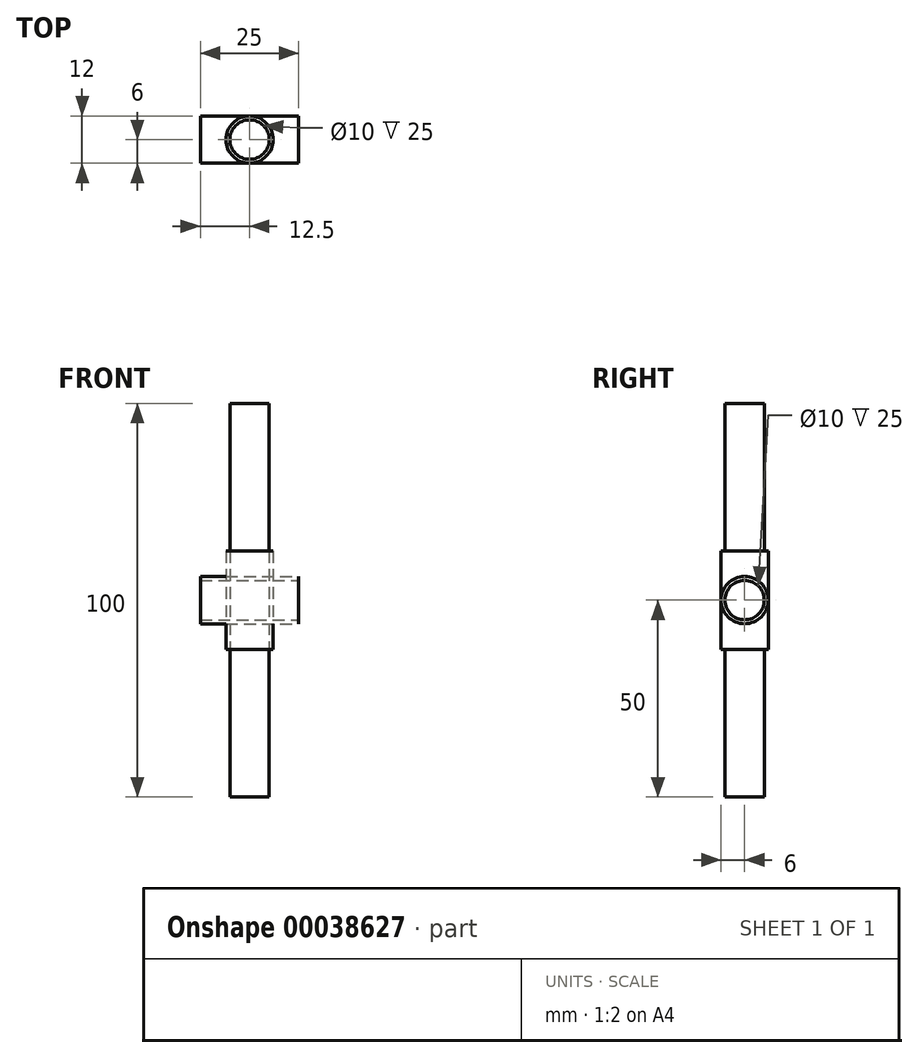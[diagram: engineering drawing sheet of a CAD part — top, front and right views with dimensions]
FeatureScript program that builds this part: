
annotation { "Feature Type Name" : "Feature", "Feature Type Description" : "" }
export const myFeature = defineFeature(function(context is Context, id is Id, definition is map)
    precondition{}
    {
        {
            var Q0;
            Q0=qCreatedBy(makeId("Top.planeOp"),FACE);
            var sketch = newSketch(context, id + "F0", { "sketchPlane" : qUnion([Q0])});
            skCircle(sketch, "E0", {"center": v(0, 0) * mm, "radius": 5 * mm});
            skCircle(sketch, "E1", {"center": v(0, 0) * mm, "radius": 6 * mm});
            skLineSegment(sketch, "E2", {"start": v(0, 0) * mm, "end": v(0, -6) * mm, "construction": true});
            skSolve(sketch);
        }
        {
            var Q0;
            Q0 = qSketchRegion(id + "F0", true);
            var Q1;
            Q1=makeQuery(id+"F0.imprint","IMPRINT",FACE,{"disambiguationData":[TD([[makeQuery(id+"F0.imprint","IMPRINT",EDGE,{"derivedFrom":sQuery(id+"F0.wireOp",EDGE,"E0")}),-1.0]])]});
            extrude(context, id + "F1", {"entities" : qUnion([Q0, Q1]), "endBound" : BoundingType.SYMMETRIC, "depth" : 25 * mm});
        }
        {
            var Q0;
            Q0=makeQuery(id+"F0.imprint","IMPRINT",FACE,{"disambiguationData":[TD([[makeQuery(id+"F0.imprint","IMPRINT",EDGE,{"derivedFrom":sQuery(id+"F0.wireOp",EDGE,"E0")}),1.0]])]});
            extrude(context, id + "F2", {"entities" : qUnion([Q0]), "endBound" : BoundingType.SYMMETRIC, "depth" : 100 * mm});
        }
        {
            var Q0;
            Q0=makeQuery(id+"F1.opExtrude","SWEPT_BODY",BODY,{"disambiguationData":[OSD([sQuery(id+"F0.wireOp",EDGE,"E0"),sQuery(id+"F0.wireOp",EDGE,"E1")])]});
            var Q1;
            Q1=sQuery(id+"F0.wireOp",EDGE,"E2");
            transform(context, id + "F3", {"entities" : qUnion([Q0]), "transformType" : TransformType.ROTATION, "transformAxis" : qUnion([Q1]), "angle" : 90 * degree, "makeCopy" : true});
        }
    });
